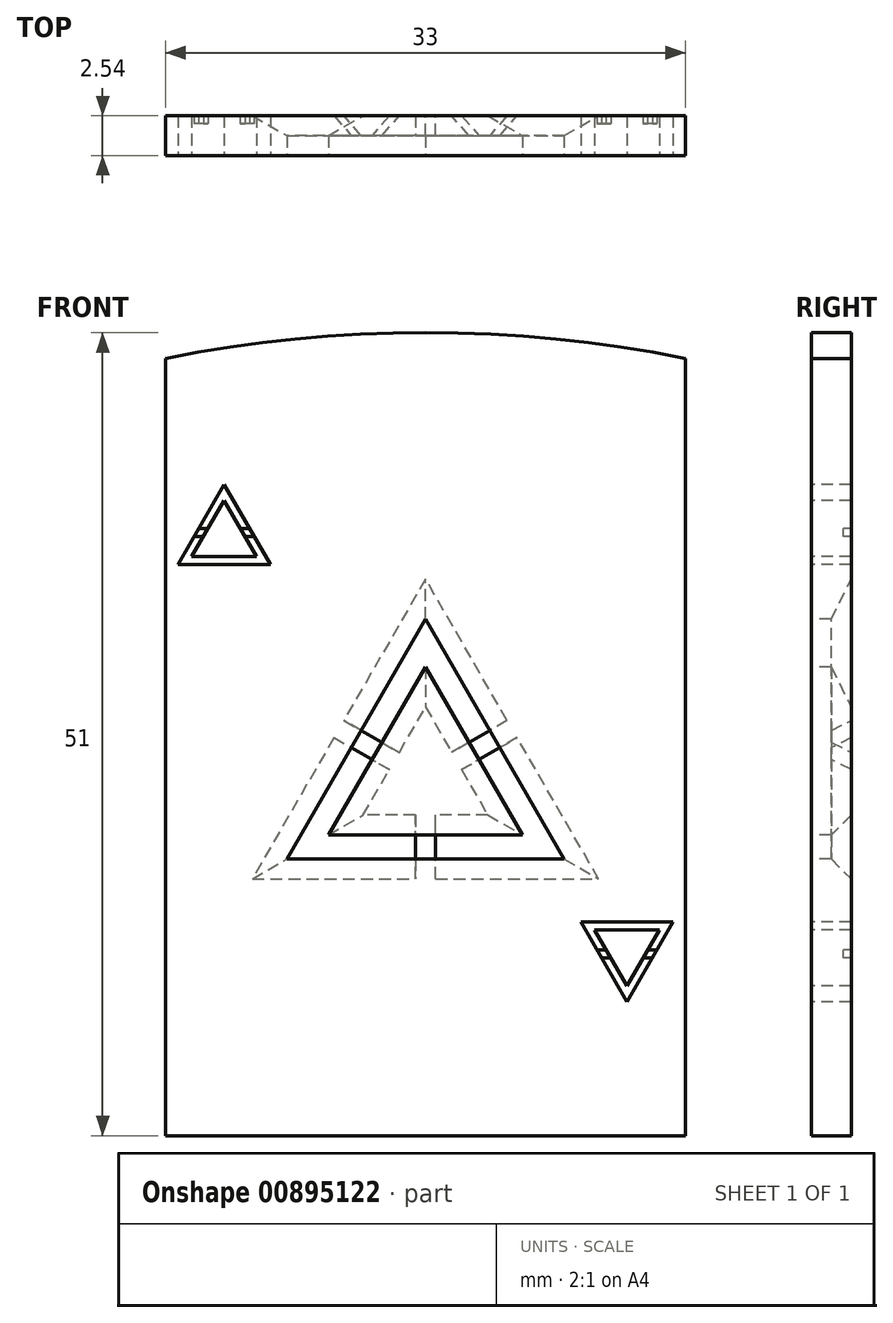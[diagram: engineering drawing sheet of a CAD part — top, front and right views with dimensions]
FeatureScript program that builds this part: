
annotation { "Feature Type Name" : "Feature", "Feature Type Description" : "" }
export const myFeature = defineFeature(function(context is Context, id is Id, definition is map)
    precondition{}
    {
        {
            var Q0;
            Q0=qCreatedBy(makeId("Front.planeOp"),FACE);
            var sketch = newSketch(context, id + "F0", { "sketchPlane" : qUnion([Q0])});
            skLineSegment(sketch, "E0", {"start": v(0, 49.37) * mm, "end": v(0, 0) * mm});
            skLineSegment(sketch, "E1", {"start": v(0, 0) * mm, "end": v(33, 0) * mm});
            skLineSegment(sketch, "E2", {"start": v(33, 0) * mm, "end": v(33, 49.37) * mm});
            skArc(sketch, "E3", {"start": v(33, 49.37) * mm, "mid": v(16.5, 51) * mm, "end": v(0, 49.37) * mm});
            skSolve(sketch);
        }
        {
            var Q0;
            Q0=qSketchRegion(id+"F0",true);
            extrude(context, id + "F1", {"entities" : qUnion([Q0]), "depth" : 2.54 * mm, "offsetDistance" : 25.4 * mm});
        }
        {
            var Q0;
            Q0=makeQuery(id+"F1.opExtrude","CAP_FACE",FACE,{"disambiguationData":[OSD([sQuery(id+"F0.wireOp",EDGE,"E0"),sQuery(id+"F0.wireOp",EDGE,"E1"),sQuery(id+"F0.wireOp",EDGE,"E2"),sQuery(id+"F0.wireOp",EDGE,"E3")])],"isStart":false});
            var sketch = newSketch(context, id + "F2", { "sketchPlane" : qUnion([Q0])});
            skLineSegment(sketch, "E4", {"start": v(16.5, 32.82) * mm, "end": v(12.42, 25.75) * mm});
            skLineSegment(sketch, "E5", {"start": v(7.7, 17.58) * mm, "end": v(15.87, 17.58) * mm});
            skLineSegment(sketch, "E6", {"start": v(25.3, 17.58) * mm, "end": v(21.22, 24.65) * mm});
            skLineSegment(sketch, "E7", {"start": v(7.7, 17.58) * mm, "end": v(0, 17.58) * mm, "construction": true});
            skLineSegment(sketch, "E8", {"start": v(25.3, 17.58) * mm, "end": v(33, 17.58) * mm, "construction": true});
            skLineSegment(sketch, "E9", {"start": v(16.5, 32.82) * mm, "end": v(16.5, 29.77) * mm, "construction": true});
            skLineSegment(sketch, "E10", {"start": v(7.7, 17.58) * mm, "end": v(10.34, 19.1) * mm, "construction": true});
            skLineSegment(sketch, "E11", {"start": v(25.3, 17.58) * mm, "end": v(22.66, 19.1) * mm, "construction": true});
            skLineSegment(sketch, "E12", {"start": v(16.5, 29.77) * mm, "end": v(13.74, 24.98) * mm});
            skLineSegment(sketch, "E13", {"start": v(22.66, 19.1) * mm, "end": v(17.14, 19.1) * mm});
            skLineSegment(sketch, "E14", {"start": v(16.5, 29.77) * mm, "end": v(19.26, 24.98) * mm});
            skLineSegment(sketch, "E15", {"start": v(16.5, 32.82) * mm, "end": v(16.5, 17.58) * mm, "construction": true});
            skPoint(sketch, "E16", {"position": v(16.5, 25.2) * mm});
            skPoint(sketch, "E17", {"position": v(0, 24.69) * mm});
            skLineSegment(sketch, "E18", {"start": v(11.78, 24.65) * mm, "end": v(13.1, 23.88) * mm});
            skLineSegment(sketch, "E19", {"start": v(12.42, 25.75) * mm, "end": v(13.74, 24.98) * mm});
            skPoint(sketch, "E20", {"position": v(12.1, 25.2) * mm});
            skPoint(sketch, "E21", {"position": v(20.9, 25.2) * mm});
            skLineSegment(sketch, "E22", {"start": v(20.58, 25.75) * mm, "end": v(19.26, 24.98) * mm});
            skLineSegment(sketch, "E23", {"start": v(21.22, 24.65) * mm, "end": v(19.9, 23.88) * mm});
            skLineSegment(sketch, "E24.trimOffspring", {"start": v(13.1, 23.88) * mm, "end": v(10.34, 19.1) * mm});
            skLineSegment(sketch, "E25.trimOffspring", {"start": v(19.9, 23.88) * mm, "end": v(22.66, 19.1) * mm});
            skLineSegment(sketch, "E26.trimOffspring", {"start": v(11.78, 24.65) * mm, "end": v(7.7, 17.58) * mm});
            skLineSegment(sketch, "E27.trimOffspring", {"start": v(20.58, 25.75) * mm, "end": v(16.5, 32.82) * mm});
            skLineSegment(sketch, "E28", {"start": v(15.87, 17.58) * mm, "end": v(15.87, 19.1) * mm});
            skLineSegment(sketch, "E29", {"start": v(17.14, 17.58) * mm, "end": v(17.14, 19.1) * mm});
            skLineSegment(sketch, "E30.trimOffspring", {"start": v(17.14, 17.58) * mm, "end": v(25.3, 17.58) * mm});
            skLineSegment(sketch, "E31.trimOffspring", {"start": v(15.87, 19.1) * mm, "end": v(10.34, 19.1) * mm});
            skLineSegment(sketch, "E32", {"start": v(26.36, 13.59) * mm, "end": v(27.39, 11.81) * mm});
            skLineSegment(sketch, "E33", {"start": v(29.3, 8.5) * mm, "end": v(30.9, 11.3) * mm});
            skLineSegment(sketch, "E34", {"start": v(29.3, 8.5) * mm, "end": v(29.3, 13.59) * mm, "construction": true});
            skLineSegment(sketch, "E35", {"start": v(29.3, 9.53) * mm, "end": v(30.32, 11.3) * mm});
            skLineSegment(sketch, "E36", {"start": v(30.32, 11.3) * mm, "end": v(30.9, 11.3) * mm});
            skLineSegment(sketch, "E37", {"start": v(29.3, 9.52) * mm, "end": v(28.27, 11.3) * mm});
            skLineSegment(sketch, "E38", {"start": v(28.27, 11.3) * mm, "end": v(27.68, 11.3) * mm});
            skLineSegment(sketch, "E39", {"start": v(27.39, 11.81) * mm, "end": v(27.97, 11.81) * mm});
            skLineSegment(sketch, "E40", {"start": v(27.97, 11.81) * mm, "end": v(27.24, 13.08) * mm});
            skLineSegment(sketch, "E41", {"start": v(29.3, 13.08) * mm, "end": v(31.34, 13.08) * mm});
            skLineSegment(sketch, "E42", {"start": v(31.34, 13.08) * mm, "end": v(30.61, 11.81) * mm});
            skLineSegment(sketch, "E43", {"start": v(30.61, 11.81) * mm, "end": v(31.2, 11.81) * mm});
            skLineSegment(sketch, "E44.trimOffspring", {"start": v(27.68, 11.3) * mm, "end": v(29.3, 8.5) * mm});
            skLineSegment(sketch, "E45.trimOffspring", {"start": v(31.2, 11.81) * mm, "end": v(32.22, 13.59) * mm});
            skLineSegment(sketch, "E46", {"start": v(32.22, 13.59) * mm, "end": v(27.83, 11.05) * mm, "construction": true});
            skLineSegment(sketch, "E47", {"start": v(26.36, 13.59) * mm, "end": v(30.76, 11.05) * mm, "construction": true});
            skLineSegment(sketch, "E48", {"start": v(26.36, 13.59) * mm, "end": v(32.22, 13.59) * mm});
            skLineSegment(sketch, "E49", {"start": v(27.24, 13.08) * mm, "end": v(29.3, 13.08) * mm});
            skLineSegment(sketch, "E50", {"start": v(0.78, 36.3) * mm, "end": v(6.64, 36.3) * mm});
            skLineSegment(sketch, "E51", {"start": v(6.64, 36.3) * mm, "end": v(3.7, 41.37) * mm, "construction": true});
            skPoint(sketch, "E51.endSnap0", {"position": v(3.7, 36.3) * mm});
            skLineSegment(sketch, "E52", {"start": v(3.7, 41.37) * mm, "end": v(0.78, 36.3) * mm, "construction": true});
            skLineSegment(sketch, "E53", {"start": v(0.78, 36.3) * mm, "end": v(1.8, 38.07) * mm});
            skLineSegment(sketch, "E54", {"start": v(1.8, 38.07) * mm, "end": v(2.39, 38.07) * mm});
            skLineSegment(sketch, "E55", {"start": v(2.39, 38.07) * mm, "end": v(1.66, 36.8) * mm});
            skLineSegment(sketch, "E56", {"start": v(1.66, 36.8) * mm, "end": v(5.76, 36.8) * mm});
            skLineSegment(sketch, "E57", {"start": v(5.76, 36.8) * mm, "end": v(5.03, 38.07) * mm});
            skLineSegment(sketch, "E58", {"start": v(5.03, 38.07) * mm, "end": v(5.61, 38.07) * mm});
            skLineSegment(sketch, "E59", {"start": v(5.61, 38.07) * mm, "end": v(6.64, 36.3) * mm});
            skLineSegment(sketch, "E60", {"start": v(3.7, 41.37) * mm, "end": v(2.1, 38.58) * mm});
            skLineSegment(sketch, "E61", {"start": v(2.1, 38.58) * mm, "end": v(2.68, 38.58) * mm});
            skLineSegment(sketch, "E62", {"start": v(2.68, 38.58) * mm, "end": v(3.7, 40.36) * mm});
            skLineSegment(sketch, "E63", {"start": v(3.7, 40.36) * mm, "end": v(4.73, 38.58) * mm});
            skLineSegment(sketch, "E64", {"start": v(4.73, 38.58) * mm, "end": v(5.32, 38.58) * mm});
            skLineSegment(sketch, "E65", {"start": v(5.32, 38.58) * mm, "end": v(3.7, 41.37) * mm});
            skSolve(sketch);
        }
        {
            var Q0;
            Q0 = qSketchRegion(id + "F2", true);
            extrude(context, id + "F3", {"entities" : qUnion([Q0]), "operationType" : NewBodyOperationType.REMOVE, "oppositeDirection" : true, "depth" : 25.4 * mm, "offsetDistance" : 25.4 * mm});
        }
        {
            var Q0;
            Q0=makeQuery(id+"F1.opExtrude","CAP_FACE",FACE,{"disambiguationData":[OSD([sQuery(id+"F0.wireOp",EDGE,"E0"),sQuery(id+"F0.wireOp",EDGE,"E1"),sQuery(id+"F0.wireOp",EDGE,"E2"),sQuery(id+"F0.wireOp",EDGE,"E3")])],"isStart":false});
            var sketch = newSketch(context, id + "F4", { "sketchPlane" : qUnion([Q0])});
            skLineSegment(sketch, "E66", {"start": v(3.7, 41.37) * mm, "end": v(0.78, 36.3) * mm});
            skLineSegment(sketch, "E67", {"start": v(0.78, 36.3) * mm, "end": v(6.64, 36.3) * mm});
            skLineSegment(sketch, "E68", {"start": v(6.64, 36.3) * mm, "end": v(3.7, 41.37) * mm});
            skLineSegment(sketch, "E69", {"start": v(3.7, 40.36) * mm, "end": v(1.66, 36.8) * mm});
            skLineSegment(sketch, "E70", {"start": v(1.66, 36.8) * mm, "end": v(5.76, 36.8) * mm});
            skLineSegment(sketch, "E71", {"start": v(5.76, 36.8) * mm, "end": v(3.7, 40.36) * mm});
            skLineSegment(sketch, "E72", {"start": v(26.36, 13.59) * mm, "end": v(29.3, 8.5) * mm});
            skLineSegment(sketch, "E73", {"start": v(29.3, 8.5) * mm, "end": v(32.22, 13.59) * mm});
            skLineSegment(sketch, "E74", {"start": v(32.22, 13.59) * mm, "end": v(26.36, 13.59) * mm});
            skLineSegment(sketch, "E75", {"start": v(27.24, 13.08) * mm, "end": v(29.3, 9.53) * mm});
            skLineSegment(sketch, "E76", {"start": v(29.3, 9.53) * mm, "end": v(31.34, 13.08) * mm});
            skLineSegment(sketch, "E77", {"start": v(31.34, 13.08) * mm, "end": v(27.24, 13.08) * mm});
            skSolve(sketch);
        }
        {
            var Q0;
            Q0 = qSketchRegion(id + "F4", true);
            extrude(context, id + "F5", {"entities" : qUnion([Q0]), "operationType" : NewBodyOperationType.REMOVE, "oppositeDirection" : true, "depth" : 2.03 * mm, "offsetDistance" : 25.4 * mm});
        }
        {
            var Q0;
            {var subQ0=sQuery(id+"F0.wireOp",EDGE,"E2");var subQ1=sQuery(id+"F0.wireOp",EDGE,"E1");var subQ2=sQuery(id+"F0.wireOp",EDGE,"E3");var subQ3=sQuery(id+"F0.wireOp",EDGE,"E0");Q0=makeQuery(id+"F5.boolean.opBoolean","SPLIT",FACE,{"disambiguationData":[TD([makeQuery(id+"F1.opExtrude","SWEPT_FACE",FACE,{"disambiguationData":[OSD([subQ3])]})])],"derivedFrom":makeQuery(id+"F1.opExtrude","CAP_FACE",FACE,{"disambiguationData":[OSD([subQ3,subQ1,subQ0,subQ2])],"isStart":false})});}
            var sketch = newSketch(context, id + "F6", { "sketchPlane" : qUnion([Q0])});
            skLineSegment(sketch, "E78", {"start": v(16.5, 32.82) * mm, "end": v(7.7, 17.58) * mm});
            skLineSegment(sketch, "E79", {"start": v(7.7, 17.58) * mm, "end": v(25.3, 17.58) * mm});
            skLineSegment(sketch, "E80", {"start": v(25.3, 17.58) * mm, "end": v(16.5, 32.82) * mm});
            skLineSegment(sketch, "E81", {"start": v(16.5, 29.77) * mm, "end": v(10.34, 19.1) * mm});
            skLineSegment(sketch, "E82", {"start": v(10.34, 19.1) * mm, "end": v(22.66, 19.1) * mm});
            skLineSegment(sketch, "E83", {"start": v(22.66, 19.1) * mm, "end": v(16.5, 29.77) * mm});
            skSolve(sketch);
        }
        {
            var Q0;
            Q0 = qSketchRegion(id + "F6", true);
            extrude(context, id + "F7", {"entities" : qUnion([Q0]), "operationType" : NewBodyOperationType.REMOVE, "oppositeDirection" : true, "depth" : 1.27 * mm, "offsetDistance" : 25.4 * mm});
        }
        {
            var Q0;
            Q0=makeQuery(id+"F3.boolean.opBoolean","INTERSECT",EDGE,{"derivedFrom":[makeQuery(id+"F1.opExtrude","CAP_FACE",FACE,{"disambiguationData":[OSD([sQuery(id+"F0.wireOp",EDGE,"E0"),sQuery(id+"F0.wireOp",EDGE,"E1"),sQuery(id+"F0.wireOp",EDGE,"E2"),sQuery(id+"F0.wireOp",EDGE,"E3")])],"isStart":true}),makeQuery(id+"F3.opExtrude","SWEPT_FACE",FACE,{"disambiguationData":[OSD([sQuery(id+"F2.wireOp",EDGE,"E27.trimOffspring")])]})]});
            var Q1;
            Q1=makeQuery(id+"F3.boolean.opBoolean","INTERSECT",EDGE,{"derivedFrom":[makeQuery(id+"F1.opExtrude","CAP_FACE",FACE,{"disambiguationData":[OSD([sQuery(id+"F0.wireOp",EDGE,"E0"),sQuery(id+"F0.wireOp",EDGE,"E1"),sQuery(id+"F0.wireOp",EDGE,"E2"),sQuery(id+"F0.wireOp",EDGE,"E3")])],"isStart":true}),makeQuery(id+"F3.opExtrude","SWEPT_FACE",FACE,{"disambiguationData":[OSD([sQuery(id+"F2.wireOp",EDGE,"E6")])]})]});
            var Q2;
            Q2=makeQuery(id+"F3.boolean.opBoolean","INTERSECT",EDGE,{"derivedFrom":[makeQuery(id+"F1.opExtrude","CAP_FACE",FACE,{"disambiguationData":[OSD([sQuery(id+"F0.wireOp",EDGE,"E0"),sQuery(id+"F0.wireOp",EDGE,"E1"),sQuery(id+"F0.wireOp",EDGE,"E2"),sQuery(id+"F0.wireOp",EDGE,"E3")])],"isStart":true}),makeQuery(id+"F3.opExtrude","SWEPT_FACE",FACE,{"disambiguationData":[OSD([sQuery(id+"F2.wireOp",EDGE,"E4")])]})]});
            var Q3;
            Q3=makeQuery(id+"F3.boolean.opBoolean","INTERSECT",EDGE,{"derivedFrom":[makeQuery(id+"F1.opExtrude","CAP_FACE",FACE,{"disambiguationData":[OSD([sQuery(id+"F0.wireOp",EDGE,"E0"),sQuery(id+"F0.wireOp",EDGE,"E1"),sQuery(id+"F0.wireOp",EDGE,"E2"),sQuery(id+"F0.wireOp",EDGE,"E3")])],"isStart":true}),makeQuery(id+"F3.opExtrude","SWEPT_FACE",FACE,{"disambiguationData":[OSD([sQuery(id+"F2.wireOp",EDGE,"E30.trimOffspring")])]})]});
            var Q4;
            Q4=makeQuery(id+"F3.boolean.opBoolean","INTERSECT",EDGE,{"derivedFrom":[makeQuery(id+"F1.opExtrude","CAP_FACE",FACE,{"disambiguationData":[OSD([sQuery(id+"F0.wireOp",EDGE,"E0"),sQuery(id+"F0.wireOp",EDGE,"E1"),sQuery(id+"F0.wireOp",EDGE,"E2"),sQuery(id+"F0.wireOp",EDGE,"E3")])],"isStart":true}),makeQuery(id+"F3.opExtrude","SWEPT_FACE",FACE,{"disambiguationData":[OSD([sQuery(id+"F2.wireOp",EDGE,"E5")])]})]});
            var Q5;
            Q5=makeQuery(id+"F3.boolean.opBoolean","INTERSECT",EDGE,{"derivedFrom":[makeQuery(id+"F1.opExtrude","CAP_FACE",FACE,{"disambiguationData":[OSD([sQuery(id+"F0.wireOp",EDGE,"E0"),sQuery(id+"F0.wireOp",EDGE,"E1"),sQuery(id+"F0.wireOp",EDGE,"E2"),sQuery(id+"F0.wireOp",EDGE,"E3")])],"isStart":true}),makeQuery(id+"F3.opExtrude","SWEPT_FACE",FACE,{"disambiguationData":[OSD([sQuery(id+"F2.wireOp",EDGE,"E26.trimOffspring")])]})]});
            var Q6;
            Q6=makeQuery(id+"F3.boolean.opBoolean","INTERSECT",EDGE,{"derivedFrom":[makeQuery(id+"F1.opExtrude","CAP_FACE",FACE,{"disambiguationData":[OSD([sQuery(id+"F0.wireOp",EDGE,"E0"),sQuery(id+"F0.wireOp",EDGE,"E1"),sQuery(id+"F0.wireOp",EDGE,"E2"),sQuery(id+"F0.wireOp",EDGE,"E3")])],"isStart":true}),makeQuery(id+"F3.opExtrude","SWEPT_FACE",FACE,{"disambiguationData":[OSD([sQuery(id+"F2.wireOp",EDGE,"E25.trimOffspring")])]})]});
            var Q7;
            Q7=makeQuery(id+"F3.boolean.opBoolean","INTERSECT",EDGE,{"derivedFrom":[makeQuery(id+"F1.opExtrude","CAP_FACE",FACE,{"disambiguationData":[OSD([sQuery(id+"F0.wireOp",EDGE,"E0"),sQuery(id+"F0.wireOp",EDGE,"E1"),sQuery(id+"F0.wireOp",EDGE,"E2"),sQuery(id+"F0.wireOp",EDGE,"E3")])],"isStart":true}),makeQuery(id+"F3.opExtrude","SWEPT_FACE",FACE,{"disambiguationData":[OSD([sQuery(id+"F2.wireOp",EDGE,"E13")])]})]});
            var Q8;
            Q8=makeQuery(id+"F3.boolean.opBoolean","INTERSECT",EDGE,{"derivedFrom":[makeQuery(id+"F1.opExtrude","CAP_FACE",FACE,{"disambiguationData":[OSD([sQuery(id+"F0.wireOp",EDGE,"E0"),sQuery(id+"F0.wireOp",EDGE,"E1"),sQuery(id+"F0.wireOp",EDGE,"E2"),sQuery(id+"F0.wireOp",EDGE,"E3")])],"isStart":true}),makeQuery(id+"F3.opExtrude","SWEPT_FACE",FACE,{"disambiguationData":[OSD([sQuery(id+"F2.wireOp",EDGE,"E31.trimOffspring")])]})]});
            var Q9;
            Q9=makeQuery(id+"F3.boolean.opBoolean","INTERSECT",EDGE,{"derivedFrom":[makeQuery(id+"F1.opExtrude","CAP_FACE",FACE,{"disambiguationData":[OSD([sQuery(id+"F0.wireOp",EDGE,"E0"),sQuery(id+"F0.wireOp",EDGE,"E1"),sQuery(id+"F0.wireOp",EDGE,"E2"),sQuery(id+"F0.wireOp",EDGE,"E3")])],"isStart":true}),makeQuery(id+"F3.opExtrude","SWEPT_FACE",FACE,{"disambiguationData":[OSD([sQuery(id+"F2.wireOp",EDGE,"E12")])]})]});
            var Q10;
            Q10=makeQuery(id+"F3.boolean.opBoolean","INTERSECT",EDGE,{"derivedFrom":[makeQuery(id+"F1.opExtrude","CAP_FACE",FACE,{"disambiguationData":[OSD([sQuery(id+"F0.wireOp",EDGE,"E0"),sQuery(id+"F0.wireOp",EDGE,"E1"),sQuery(id+"F0.wireOp",EDGE,"E2"),sQuery(id+"F0.wireOp",EDGE,"E3")])],"isStart":true}),makeQuery(id+"F3.opExtrude","SWEPT_FACE",FACE,{"disambiguationData":[OSD([sQuery(id+"F2.wireOp",EDGE,"E14")])]})]});
            var Q11;
            Q11=makeQuery(id+"F3.boolean.opBoolean","INTERSECT",EDGE,{"derivedFrom":[makeQuery(id+"F1.opExtrude","CAP_FACE",FACE,{"disambiguationData":[OSD([sQuery(id+"F0.wireOp",EDGE,"E0"),sQuery(id+"F0.wireOp",EDGE,"E1"),sQuery(id+"F0.wireOp",EDGE,"E2"),sQuery(id+"F0.wireOp",EDGE,"E3")])],"isStart":true}),makeQuery(id+"F3.opExtrude","SWEPT_FACE",FACE,{"disambiguationData":[OSD([sQuery(id+"F2.wireOp",EDGE,"E24.trimOffspring")])]})]});
            chamfer(context, id + "F8", {"entities" : qUnion([Q0, Q1, Q2, Q3, Q4, Q5, Q6, Q7, Q8, Q9, Q10, Q11]), "width" : 1.27 * mm, "tangentPropagation" : true});
        }
    });
